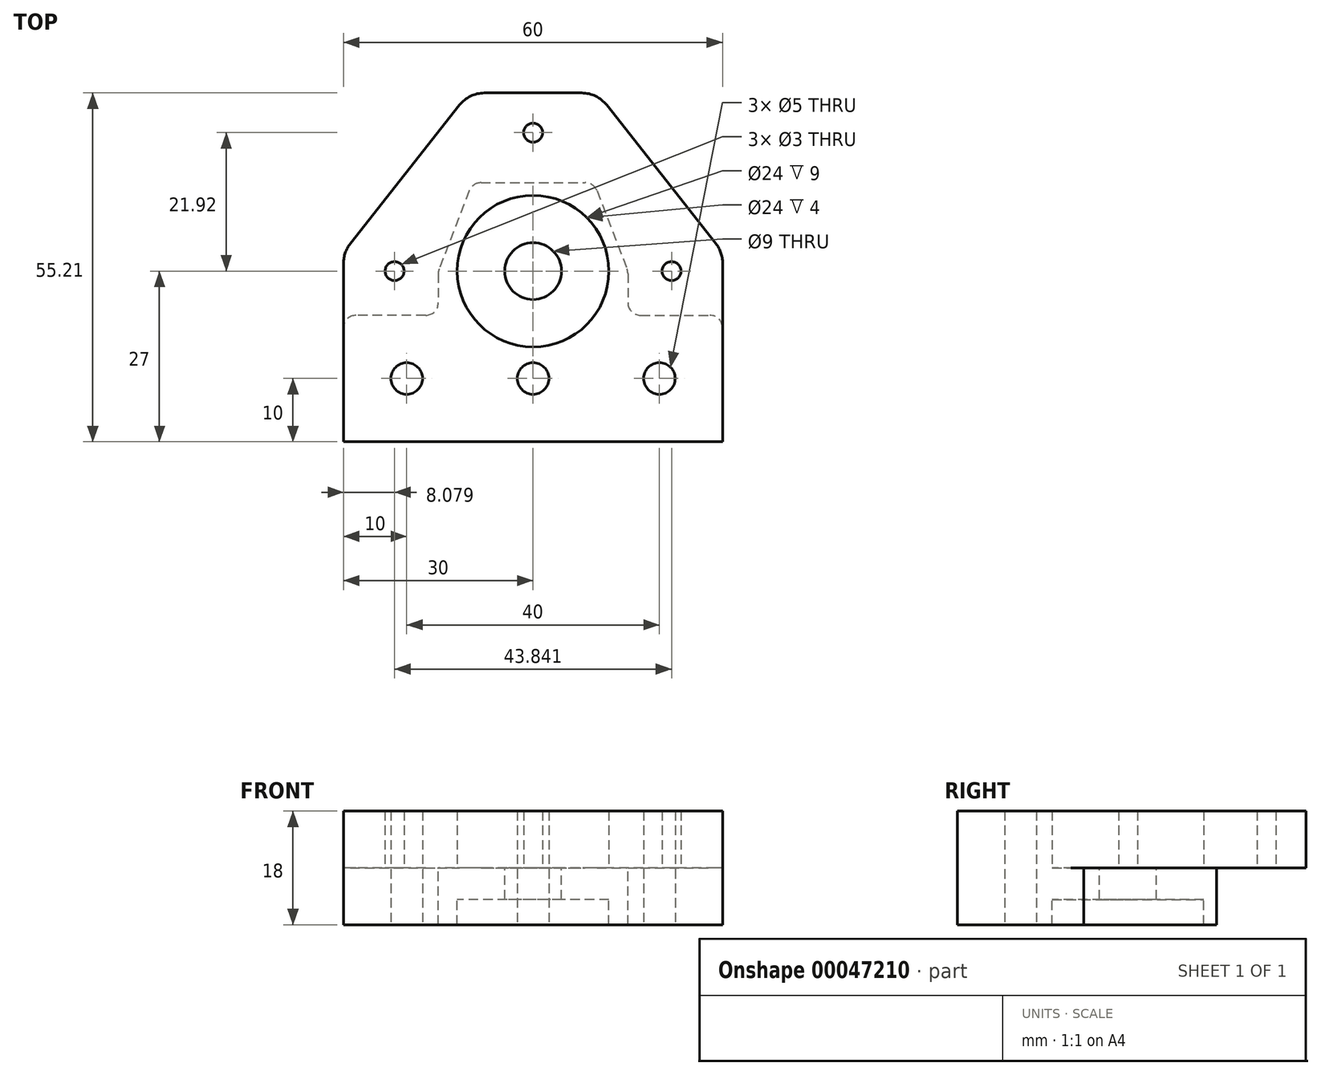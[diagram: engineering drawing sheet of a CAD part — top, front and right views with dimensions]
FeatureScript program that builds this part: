
annotation { "Feature Type Name" : "Feature", "Feature Type Description" : "" }
export const myFeature = defineFeature(function(context is Context, id is Id, definition is map)
    precondition{}
    {
        {
            var Q0;
            Q0=qCreatedBy(makeId("Top.planeOp"),FACE);
            var sketch = newSketch(context, id + "F0", { "sketchPlane" : qUnion([Q0])});
            skCircle(sketch, "E0", {"center": v(-21.92, 0) * mm, "radius": 1.5 * mm});
            skCircle(sketch, "E1", {"center": v(0, 0) * mm, "radius": 12 * mm});
            skCircle(sketch, "E2.MirrorC", {"center": v(21.92, 0) * mm, "radius": 1.5 * mm});
            skLineSegment(sketch, "E3.bottom", {"start": v(-10.14, 28.21) * mm, "end": v(7.7, 28.21) * mm});
            skLineSegment(sketch, "E3.top", {"start": v(-30, -27) * mm, "end": v(30, -27) * mm});
            skLineSegment(sketch, "E3.left", {"start": v(-30, 0) * mm, "end": v(-30, -27) * mm});
            skLineSegment(sketch, "E3.right", {"start": v(30, 0) * mm, "end": v(30, -27) * mm});
            skCircle(sketch, "E4", {"center": v(-20, -17) * mm, "radius": 2.5 * mm});
            skCircle(sketch, "E5", {"center": v(0, -17) * mm, "radius": 2.5 * mm});
            skPoint(sketch, "E6.visualSharp", {"position": v(-30, 28.21) * mm});
            skPoint(sketch, "E7.visualSharp", {"position": v(30, 28.21) * mm});
            skCircle(sketch, "E8.MirrorC", {"center": v(20, -17) * mm, "radius": 2.5 * mm});
            skCircle(sketch, "E9", {"center": v(0, 0) * mm, "radius": 4.5 * mm});
            skLineSegment(sketch, "E10", {"start": v(-1.44, 28.21) * mm, "end": v(-7.7, 28.21) * mm});
            skPoint(sketch, "E6.filletArc.start.orphan", {"position": v(-1.44, 28.21) * mm});
            skLineSegment(sketch, "E11", {"start": v(-30, 0) * mm, "end": v(-30, 1.27) * mm});
            skLineSegment(sketch, "E12", {"start": v(-28.93, 4.36) * mm, "end": v(-11.64, 26.3) * mm});
            skLineSegment(sketch, "E13.MirrorCS", {"start": v(28.93, 4.36) * mm, "end": v(11.64, 26.3) * mm});
            skLineSegment(sketch, "E14.MirrorCS", {"start": v(30, 0) * mm, "end": v(30, 1.27) * mm});
            skPoint(sketch, "E15.visualSharp", {"position": v(-10.14, 28.21) * mm});
            skArc(sketch, "E15.filletArc", {"start": v(-7.7, 28.21) * mm, "mid": v(-9.9, 27.7) * mm, "end": v(-11.64, 26.3) * mm});
            skPoint(sketch, "E16.visualSharp", {"position": v(-30, 3) * mm});
            skArc(sketch, "E16.filletArc", {"start": v(-28.93, 4.36) * mm, "mid": v(-29.72, 2.9) * mm, "end": v(-30, 1.27) * mm});
            skPoint(sketch, "E17.visualSharp", {"position": v(10.14, 28.21) * mm});
            skArc(sketch, "E17.filletArc", {"start": v(11.64, 26.3) * mm, "mid": v(9.9, 27.7) * mm, "end": v(7.7, 28.21) * mm});
            skPoint(sketch, "E18.visualSharp", {"position": v(30, 3) * mm});
            skArc(sketch, "E18.filletArc", {"start": v(30, 1.27) * mm, "mid": v(29.72, 2.9) * mm, "end": v(28.93, 4.36) * mm});
            skCircle(sketch, "E19", {"center": v(0, 21.92) * mm, "radius": 1.5 * mm});
            skSolve(sketch);
        }
        {
            var Q0;
            Q0=qCreatedBy(makeId("Top.planeOp"),FACE);
            var sketch = newSketch(context, id + "F1", { "sketchPlane" : qUnion([Q0])});
            skCircle(sketch, "E20", {"center": v(0, 0) * mm, "radius": 4.5 * mm});
            skLineSegment(sketch, "E21", {"start": v(-30, -9) * mm, "end": v(-30, -27) * mm});
            skLineSegment(sketch, "E22", {"start": v(-30, -27) * mm, "end": v(30, -27) * mm});
            skLineSegment(sketch, "E23", {"start": v(30, -27) * mm, "end": v(30, -7) * mm});
            skCircle(sketch, "E24", {"center": v(-20, -17) * mm, "radius": 2.5 * mm});
            skCircle(sketch, "E25", {"center": v(0, -17) * mm, "radius": 2.5 * mm});
            skCircle(sketch, "E26.MirrorC", {"center": v(20, -17) * mm, "radius": 2.5 * mm});
            skCircle(sketch, "E27", {"center": v(0, 0) * mm, "radius": 12 * mm});
            skLineSegment(sketch, "E28", {"start": v(0, 14) * mm, "end": v(-8.24, 14) * mm});
            skLineSegment(sketch, "E29", {"start": v(-10.1, 12.72) * mm, "end": v(-14.87, 0.35) * mm});
            skLineSegment(sketch, "E30", {"start": v(-15, -0.37) * mm, "end": v(-15, -5) * mm});
            skLineSegment(sketch, "E31", {"start": v(-17, -7) * mm, "end": v(-28, -7) * mm});
            skPoint(sketch, "E32.visualSharp", {"position": v(-9.61, 14) * mm});
            skArc(sketch, "E32.filletArc", {"start": v(-8.24, 14) * mm, "mid": v(-9.37, 13.65) * mm, "end": v(-10.1, 12.72) * mm});
            skPoint(sketch, "E33.visualSharp", {"position": v(-15, 0) * mm});
            skArc(sketch, "E33.filletArc", {"start": v(-14.87, 0.35) * mm, "mid": v(-14.97, 0) * mm, "end": v(-15, -0.37) * mm});
            skPoint(sketch, "E34.visualSharp", {"position": v(-15, -7) * mm});
            skArc(sketch, "E34.filletArc", {"start": v(-17, -7) * mm, "mid": v(-15.59, -6.41) * mm, "end": v(-15, -5) * mm});
            skPoint(sketch, "E35.visualSharp", {"position": v(-30, -7) * mm});
            skArc(sketch, "E35.filletArc", {"start": v(-28, -7) * mm, "mid": v(-29.41, -7.59) * mm, "end": v(-30, -9) * mm});
            skArc(sketch, "E36.MirrorCS", {"start": v(8.24, 14) * mm, "mid": v(9.37, 13.65) * mm, "end": v(10.1, 12.72) * mm});
            skLineSegment(sketch, "E37.MirrorCS", {"start": v(0, 14) * mm, "end": v(8.24, 14) * mm});
            skPoint(sketch, "E38.MirrorP", {"position": v(9.61, 14) * mm});
            skLineSegment(sketch, "E39.MirrorCS", {"start": v(10.1, 12.72) * mm, "end": v(14.87, 0.35) * mm});
            skArc(sketch, "E40.MirrorCS", {"start": v(14.87, 0.35) * mm, "mid": v(14.97, 0) * mm, "end": v(15, -0.37) * mm});
            skLineSegment(sketch, "E41.MirrorCS", {"start": v(15, -0.37) * mm, "end": v(15, -5) * mm});
            skPoint(sketch, "E42.MirrorP", {"position": v(15, 0) * mm});
            skPoint(sketch, "E43.MirrorP", {"position": v(15, -7) * mm});
            skPoint(sketch, "E44.MirrorP", {"position": v(30, -7) * mm});
            skLineSegment(sketch, "E45.MirrorCS", {"start": v(17, -7) * mm, "end": v(28, -7) * mm});
            skArc(sketch, "E46.MirrorCS", {"start": v(28, -7) * mm, "mid": v(29.41, -7.59) * mm, "end": v(30, -9) * mm});
            skArc(sketch, "E47.MirrorCS", {"start": v(17, -7) * mm, "mid": v(15.59, -6.41) * mm, "end": v(15, -5) * mm});
            skSolve(sketch);
        }
        {
            var Q0;
            Q0 = qSketchRegion(id + "F0", true);
            extrude(context, id + "F2", {"entities" : qUnion([Q0]), "depth" : 9 * mm});
        }
        {
            var Q0;
            Q0=makeQuery(id+"F1.imprint","IMPRINT",FACE,{"disambiguationData":[TD([[makeQuery(id+"F1.imprint","IMPRINT",EDGE,{"derivedFrom":sQuery(id+"F1.wireOp",EDGE,"E21")}),1.0]])]});
            extrude(context, id + "F3", {"entities" : qUnion([Q0]), "oppositeDirection" : true, "depth" : 9 * mm});
        }
        {
            var Q0;
            Q0=makeQuery(id+"F1.imprint","IMPRINT",FACE,{"disambiguationData":[TD([[makeQuery(id+"F1.imprint","IMPRINT",EDGE,{"derivedFrom":sQuery(id+"F1.wireOp",EDGE,"E20")}),-1.0]])]});
            extrude(context, id + "F4", {"entities" : qUnion([Q0]), "operationType" : NewBodyOperationType.ADD, "oppositeDirection" : true, "depth" : 5 * mm});
        }
    });
